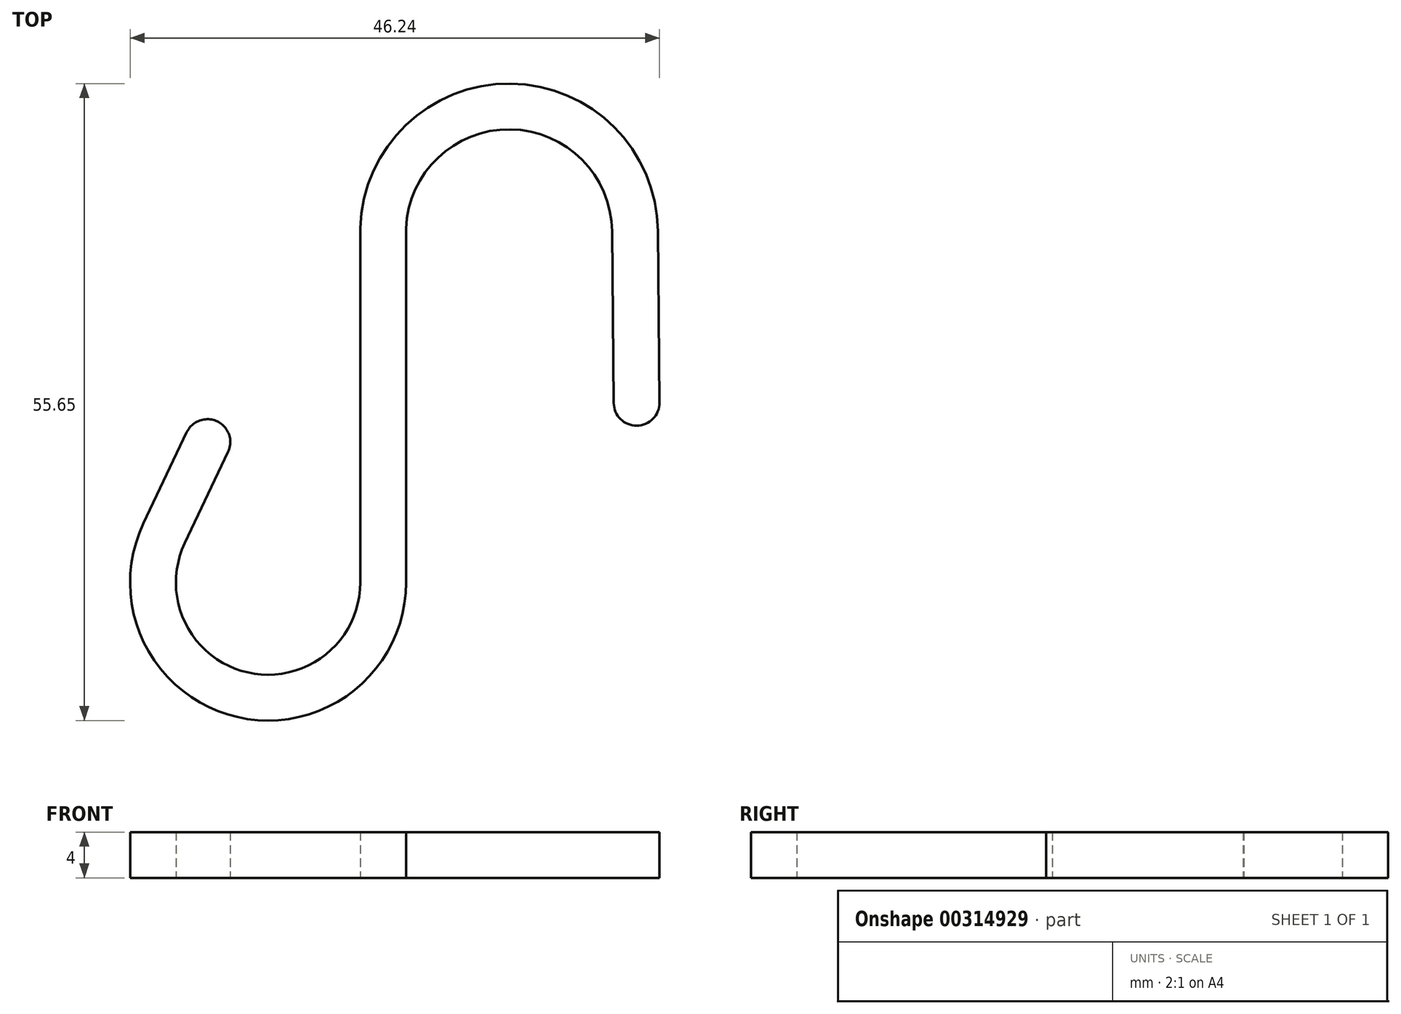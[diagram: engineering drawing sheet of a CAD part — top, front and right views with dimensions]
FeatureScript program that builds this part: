
annotation { "Feature Type Name" : "Feature", "Feature Type Description" : "" }
export const myFeature = defineFeature(function(context is Context, id is Id, definition is map)
    precondition{}
    {
        {
            var Q0;
            Q0=qCreatedBy(makeId("Top.planeOp"),FACE);
            var sketch = newSketch(context, id + "F0", { "sketchPlane" : qUnion([Q0])});
            skArc(sketch, "E0", {"start": v(-3.12, 34.34) * mm, "mid": v(-16, 47.21) * mm, "end": v(-29.12, 34.6) * mm});
            skLineSegment(sketch, "E1", {"start": v(-3.12, 34.34) * mm, "end": v(-2.98, 19.34) * mm});
            skLineSegment(sketch, "E2", {"start": v(-29.12, 34.6) * mm, "end": v(-29.12, 3.6) * mm});
            skArc(sketch, "E3", {"start": v(-44.44, 7.06) * mm, "mid": v(-38.94, -4.25) * mm, "end": v(-29.12, 3.6) * mm});
            skLineSegment(sketch, "E4", {"start": v(-44.44, 7.06) * mm, "end": v(-40.66, 15.03) * mm});
            skLineSegment(sketch, "E5.0", {"start": v(-48.06, 8.77) * mm, "end": v(-44.27, 16.74) * mm});
            skLineSegment(sketch, "E5.1", {"start": v(-7.12, 34.3) * mm, "end": v(-6.98, 19.3) * mm});
            skArc(sketch, "E5.2", {"start": v(-7.12, 34.3) * mm, "mid": v(-16, 43.21) * mm, "end": v(-25.12, 34.54) * mm});
            skLineSegment(sketch, "E5.3", {"start": v(-25.12, 34.54) * mm, "end": v(-25.12, 3.6) * mm});
            skArc(sketch, "E5.4", {"start": v(-48.06, 8.77) * mm, "mid": v(-39.82, -8.15) * mm, "end": v(-25.12, 3.6) * mm});
            skArc(sketch, "E6", {"start": v(-44.27, 16.74) * mm, "mid": v(-41.61, 17.7) * mm, "end": v(-40.66, 15.03) * mm});
            skArc(sketch, "E7", {"start": v(-6.98, 19.3) * mm, "mid": v(-4.96, 17.32) * mm, "end": v(-2.98, 19.34) * mm});
            skSolve(sketch);
        }
        {
            var Q0;
            Q0=makeQuery(id+"F0.imprint","IMPRINT",FACE,{"disambiguationData":[TD([[makeQuery(id+"F0.imprint","IMPRINT",EDGE,{"derivedFrom":sQuery(id+"F0.wireOp",EDGE,"E0")}),1.0]])]});
            extrude(context, id + "F1", {"entities" : qUnion([Q0]), "depth" : 4 * mm});
        }
    });
